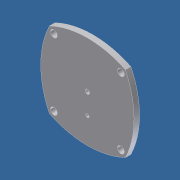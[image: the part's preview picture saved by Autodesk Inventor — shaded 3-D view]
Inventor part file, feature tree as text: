
AUTODESK INVENTOR PART (.ipt)
format: ipt  version: unknown  size: 222,208 bytes
history: native  units: in
note: dims shown in document units (in); Inventor stores cm internally (conversion verified against a paired STEP export)
features: extrude x3, sketch x2, revolve x1
ambient origin geometry x8: Origin, YZ Plane, XZ Plane, XY Plane, X Axis, Y Axis, Z Axis, Center Point
bodies: Solid1 (feature_tree)
feature tree (6):
  extrude  "Extrusion1"  Depth=0.25in
  sketch  "Sketch2"  dims[d2=2.425in d3=2.75in d4=0.1625in d5=0.1625in d6=3.375in d7=0.2in d8=0.0in d10=0.075in d11=1.4in d12=0.25in d13=0.1in d14=0.0in d15=0.1625in d16=0.1in d17=0.0in d18=0.125in d19=0.75in d21=0.675in d22=0.35in d23=90.0deg]
  extrude  "Extrusion2"  Depth=2.75in
  extrude  "Extrusion3"  Depth=0.1625in
  revolve  "Revolution1"  [1 undecoded]
  sketch  "Sketch1"  dims[d0=2.425in d1=0.25in]
note: 1 required parameter value undecoded (feature->parameter linkage not recoverable at this tier; creation-order binding heuristic only, values carry confidence <= 0.55)
